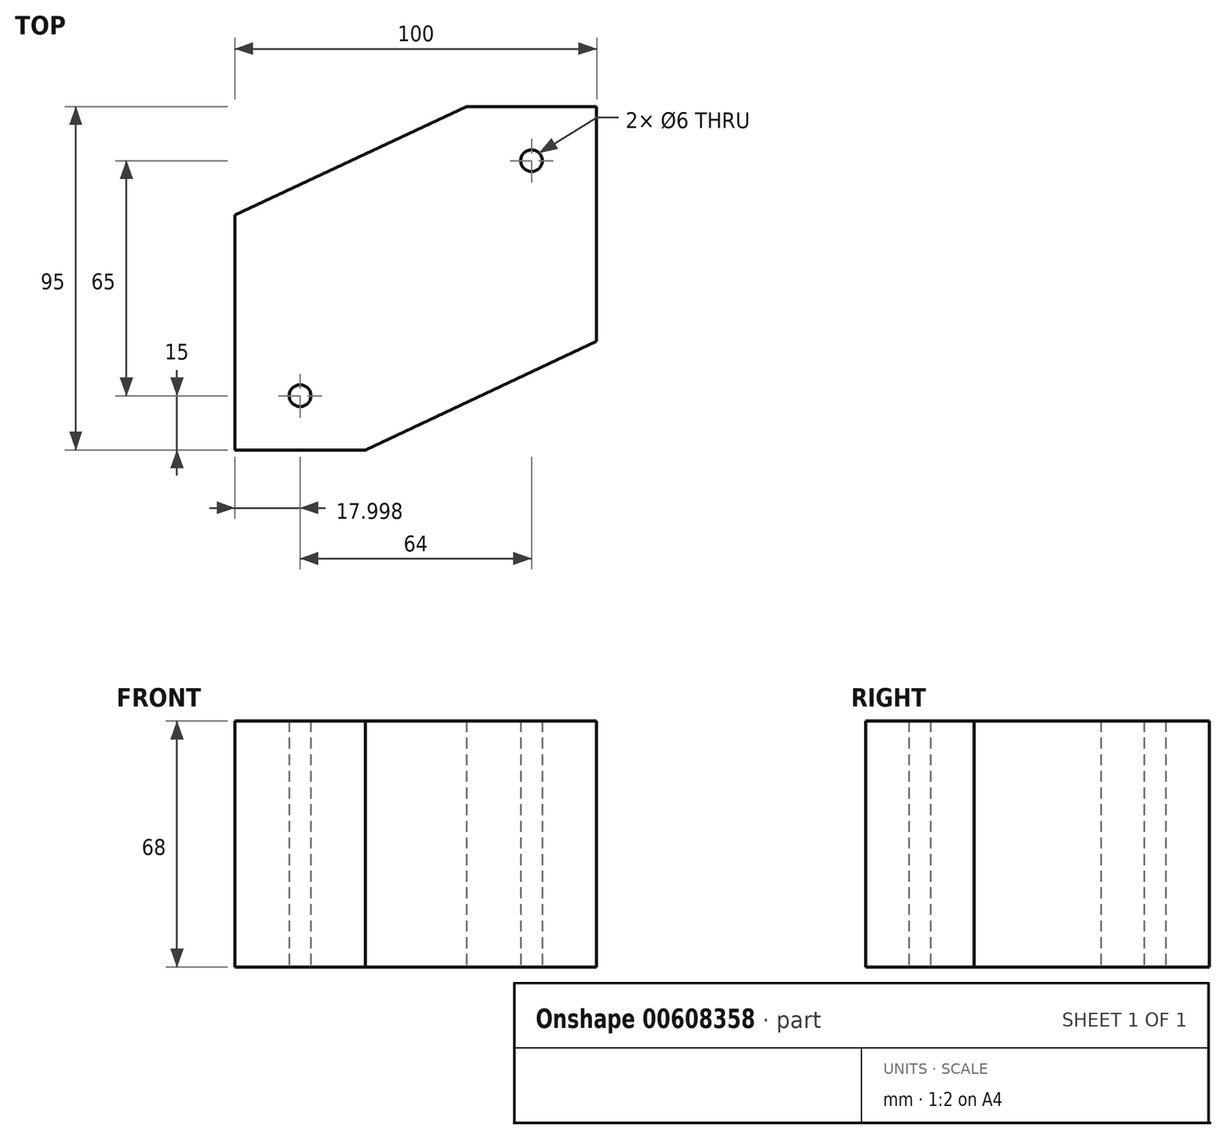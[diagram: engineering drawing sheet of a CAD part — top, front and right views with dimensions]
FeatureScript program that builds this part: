
annotation { "Feature Type Name" : "Feature", "Feature Type Description" : "" }
export const myFeature = defineFeature(function(context is Context, id is Id, definition is map)
    precondition{}
    {
        {
            var Q0;
            Q0=qCreatedBy(makeId("Top.planeOp"),FACE);
            var sketch = newSketch(context, id + "F0", { "sketchPlane" : qUnion([Q0])});
            skLineSegment(sketch, "E0", {"start": v(47.54, 50) * mm, "end": v(47.54, -15) * mm});
            skLineSegment(sketch, "E1", {"start": v(-52.46, -45) * mm, "end": v(-52.46, 20) * mm});
            skLineSegment(sketch, "E2.bottom", {"start": v(47.54, -2.5) * mm, "end": v(-52.46, -2.5) * mm, "construction": true});
            skLineSegment(sketch, "E2.top", {"start": v(47.54, 7.5) * mm, "end": v(-52.46, 7.5) * mm, "construction": true});
            skPoint(sketch, "E2.middle", {"position": v(-2.46, 2.5) * mm});
            skCircle(sketch, "E3", {"center": v(29.54, 35) * mm, "radius": 3 * mm});
            skCircle(sketch, "E4", {"center": v(-34.46, -30) * mm, "radius": 3 * mm});
            skLineSegment(sketch, "E5", {"start": v(-52.46, 20) * mm, "end": v(11.54, 50) * mm});
            skLineSegment(sketch, "E6", {"start": v(11.54, 50) * mm, "end": v(47.54, 50) * mm});
            skLineSegment(sketch, "E7", {"start": v(-52.46, -45) * mm, "end": v(-16.46, -45) * mm});
            skLineSegment(sketch, "E8", {"start": v(-16.46, -45) * mm, "end": v(47.54, -15) * mm});
            skLineSegment(sketch, "E9", {"start": v(-34.46, -30) * mm, "end": v(29.54, -30) * mm, "construction": true});
            skLineSegment(sketch, "E10", {"start": v(29.54, -30) * mm, "end": v(29.54, 35) * mm, "construction": true});
            skSolve(sketch);
        }
        {
            var Q0;
            Q0=makeQuery(id+"F0.imprint","IMPRINT",FACE,{"disambiguationData":[TD([[makeQuery(id+"F0.imprint","IMPRINT",EDGE,{"derivedFrom":sQuery(id+"F0.wireOp",EDGE,"E0")}),-1.0]])]});
            extrude(context, id + "F1", {"entities" : qUnion([Q0]), "endBound" : BoundingType.SYMMETRIC, "depth" : 68 * mm, "offsetDistance" : 25 * mm});
        }
    });
